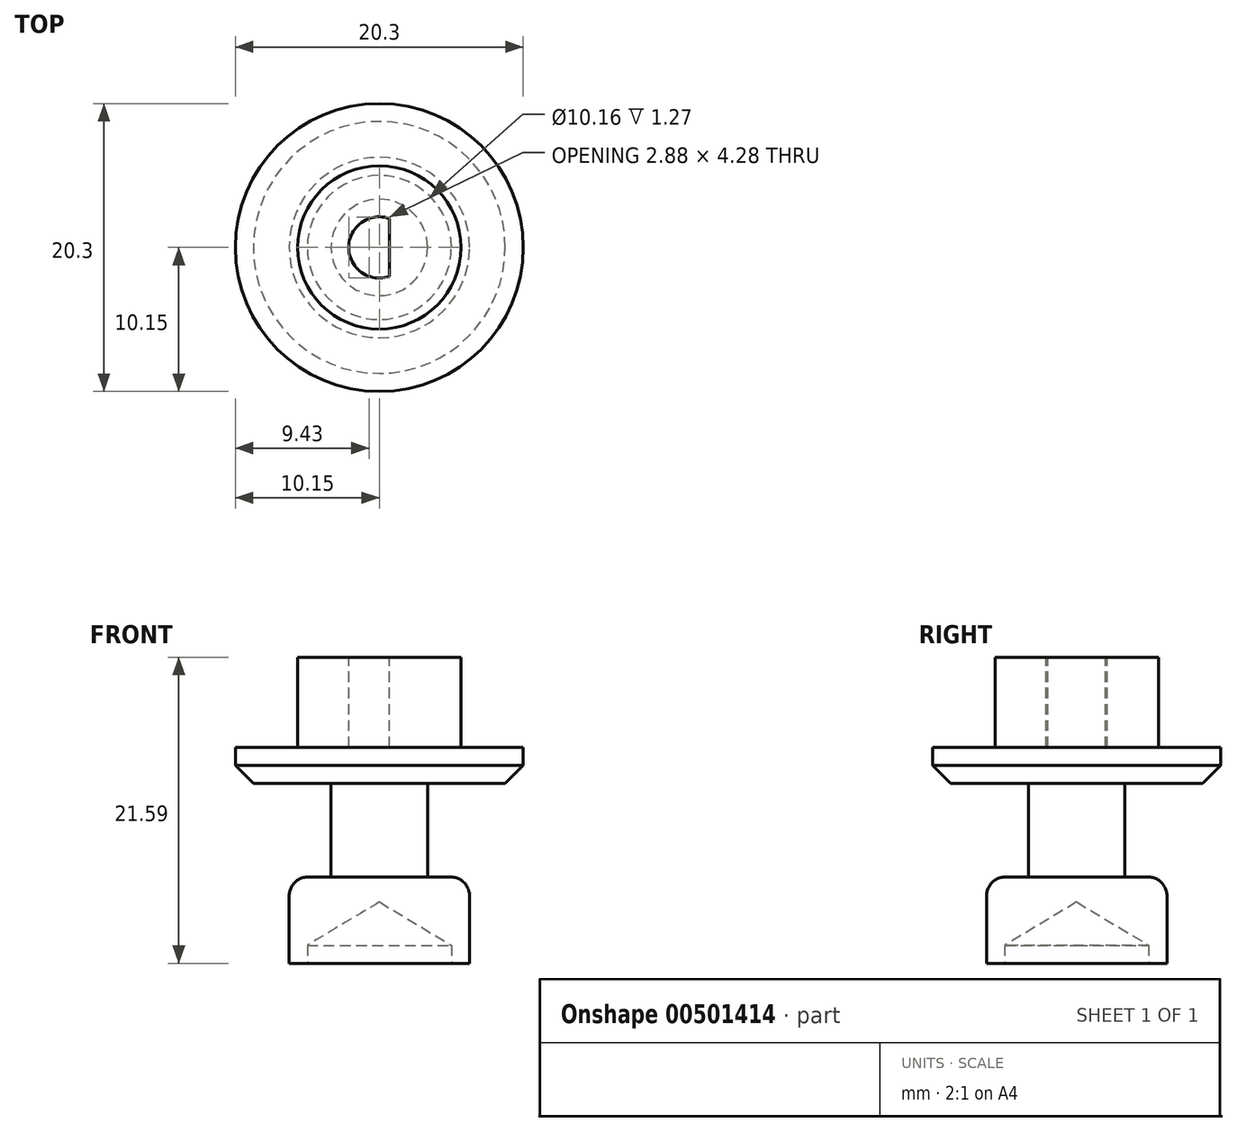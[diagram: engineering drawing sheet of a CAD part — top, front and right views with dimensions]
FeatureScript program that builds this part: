
annotation { "Feature Type Name" : "Feature", "Feature Type Description" : "" }
export const myFeature = defineFeature(function(context is Context, id is Id, definition is map)
    precondition{}
    {
        {
            var Q0;
            Q0=qCreatedBy(makeId("Top.planeOp"),FACE);
            var sketch = newSketch(context, id + "F0", { "sketchPlane" : qUnion([Q0])});
            skCircle(sketch, "E0", {"center": v(0, 0) * mm, "radius": 6.36 * mm});
            skSolve(sketch);
        }
        {
            var Q0;
            Q0=qSketchRegion(id+"F0",true);
            extrude(context, id + "F1", {"entities" : qUnion([Q0]), "depth" : 6.1 * mm});
        }
        {
            var Q0;
            Q0=qCreatedBy(makeId("Top.planeOp"),FACE);
            var sketch = newSketch(context, id + "F2", { "sketchPlane" : qUnion([Q0])});
            skCircle(sketch, "E1", {"center": v(0, 0) * mm, "radius": 3.4 * mm});
            skSolve(sketch);
        }
        {
            var Q0;
            Q0=qSketchRegion(id+"F2",true);
            extrude(context, id + "F3", {"entities" : qUnion([Q0]), "operationType" : NewBodyOperationType.ADD, "depth" : 12.7 * mm});
        }
        {
            var Q0;
            Q0=makeQuery(id+"F3.opExtrude","CAP_FACE",FACE,{"disambiguationData":[OSD([sQuery(id+"F2.wireOp",EDGE,"E1")])],"isStart":false});
            cPlane(context, id + "F4", {"entities" : qUnion([Q0]), "cplaneType" : CPlaneType.OFFSET, "offset" : 0 * mm, "width" : 152.4 * mm, "height" : 152.4 * mm});
        }
        {
            var Q0;
            Q0=qCreatedBy(id+"F4.planeOp",FACE);
            var sketch = newSketch(context, id + "F5", { "sketchPlane" : qUnion([Q0])});
            skCircle(sketch, "E2", {"center": v(0, 0) * mm, "radius": 10.15 * mm});
            skSolve(sketch);
        }
        {
            var Q0;
            Q0=qSketchRegion(id+"F5",true);
            extrude(context, id + "F6", {"entities" : qUnion([Q0]), "operationType" : NewBodyOperationType.ADD, "depth" : 2.54 * mm});
        }
        {
            var Q0;
            Q0=makeQuery(id+"F6.opExtrude","CAP_FACE",FACE,{"disambiguationData":[OSD([sQuery(id+"F5.wireOp",EDGE,"E2")])],"isStart":false});
            cPlane(context, id + "F7", {"entities" : qUnion([Q0]), "cplaneType" : CPlaneType.OFFSET, "offset" : 0 * mm, "width" : 152.4 * mm, "height" : 152.4 * mm});
        }
        {
            var Q0;
            Q0=qCreatedBy(id+"F7.planeOp",FACE);
            var sketch = newSketch(context, id + "F8", { "sketchPlane" : qUnion([Q0])});
            skCircle(sketch, "E3", {"center": v(0, 0) * mm, "radius": 5.76 * mm});
            skSolve(sketch);
        }
        {
            var Q0;
            Q0=qSketchRegion(id+"F8",true);
            extrude(context, id + "F9", {"entities" : qUnion([Q0]), "depth" : 6.35 * mm});
        }
        {
            var Q0;
            Q0=makeQuery(id+"F9.opExtrude","CAP_FACE",FACE,{"disambiguationData":[OSD([sQuery(id+"F8.wireOp",EDGE,"E3")])],"isStart":false});
            cPlane(context, id + "F10", {"entities" : qUnion([Q0]), "cplaneType" : CPlaneType.OFFSET, "offset" : 0 * mm, "width" : 152.4 * mm, "height" : 152.4 * mm});
        }
        {
            var Q0;
            Q0=qCreatedBy(id+"F10.planeOp",FACE);
            var sketch = newSketch(context, id + "F11", { "sketchPlane" : qUnion([Q0])});
            skCircle(sketch, "E4", {"center": v(0, 0) * mm, "radius": 2.16 * mm});
            skLineSegment(sketch, "E5", {"start": v(0.72, 0) * mm, "end": v(0.72, 2.04) * mm});
            skLineSegment(sketch, "E6", {"start": v(0.72, 2.04) * mm, "end": v(0.72, -2.04) * mm});
            skSolve(sketch);
        }
        {
            var Q0;
            {var subQ0=sQuery(id+"F11.wireOp",EDGE,"E6");var subQ4=makeQuery(id+"F11.imprint","IMPRINT",VERTEX,{"derivedFrom":subQ0});Q0=makeQuery(id+"F11.imprint","IMPRINT",FACE,{"disambiguationData":[TD([[makeQuery(id+"F11.imprint","IMPRINT",EDGE,{"disambiguationData":[TD([[subQ4,1.0]])],"derivedFrom":subQ0}),-1.0]])]});}
            extrude(context, id + "F12", {"entities" : qUnion([Q0]), "operationType" : NewBodyOperationType.REMOVE, "oppositeDirection" : true, "depth" : 6.35 * mm});
        }
        {
            var Q0;
            Q0=sQuery(id+"F0.wireOp",VERTEX,"E0.center");
            var Q1;
            Q1=makeQuery(id+"F1.opExtrude","SWEPT_BODY",BODY,{"disambiguationData":[OSD([sQuery(id+"F0.wireOp",EDGE,"E0")])]});
            hole(context, id + "F13", {"style" : HoleStyle.SIMPLE, "endStyle" : HoleEndStyle.BLIND, "oppositeDirection" : true, "holeDiameter" : 10.16 * mm, "holeDepth" : 1.27 * mm, "isTappedThrough" : true, "tappedDepth" : 12.7 * mm, "tapClearance" : 3, "locations" : qUnion([Q0]), "scope" : qUnion([Q1])});
        }
        {
            var Q0;
            Q0=makeQuery(id+"F1.opExtrude","CAP_EDGE",EDGE,{"disambiguationData":[OSD([sQuery(id+"F0.wireOp",EDGE,"E0")])],"isStart":false});
            fillet(context, id + "F14", {"entities" : qUnion([Q0]), "radius" : 1.35 * mm, "tangentPropagation" : true, "allowEdgeOverflow" : false});
        }
        {
            var Q0;
            Q0=makeQuery(id+"F6.opExtrude","CAP_EDGE",EDGE,{"disambiguationData":[OSD([sQuery(id+"F5.wireOp",EDGE,"E2")])],"isStart":true});
            chamfer(context, id + "F15", {"entities" : qUnion([Q0]), "width" : 1.27 * mm, "tangentPropagation" : true});
        }
    });
